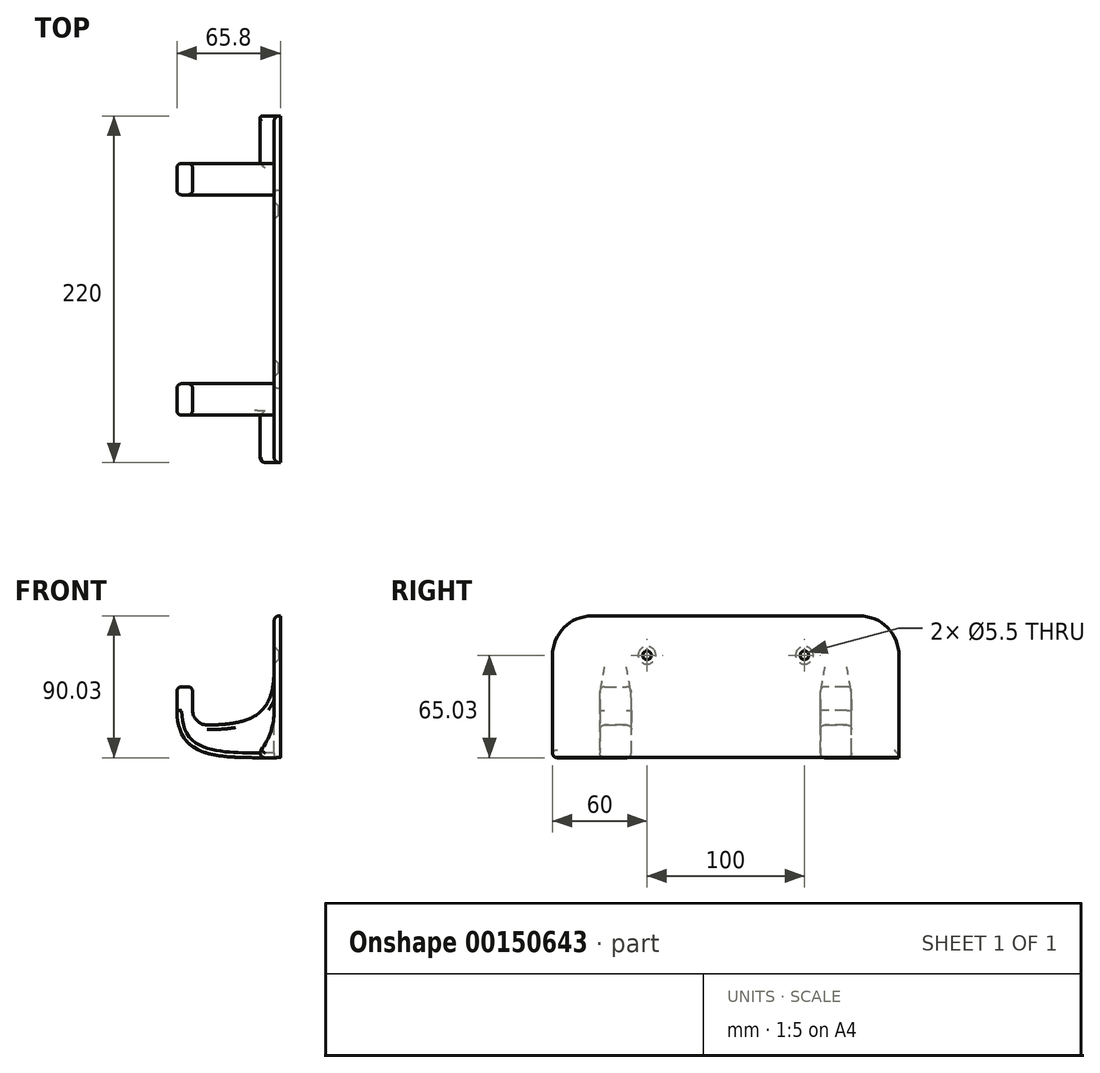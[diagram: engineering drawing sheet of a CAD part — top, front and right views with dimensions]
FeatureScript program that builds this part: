
annotation { "Feature Type Name" : "Feature", "Feature Type Description" : "" }
export const myFeature = defineFeature(function(context is Context, id is Id, definition is map)
    precondition{}
    {
        {
            var Q0;
            Q0=qCreatedBy(makeId("Front.planeOp"),FACE);
            var sketch = newSketch(context, id + "F0", { "sketchPlane" : qUnion([Q0])});
            skCircle(sketch, "E0", {"center": v(0, 0) * mm, "radius": 42.6 * mm});
            skLineSegment(sketch, "E1.bottom", {"start": v(36.6, 60) * mm, "end": v(46.6, 60) * mm});
            skLineSegment(sketch, "E1.top", {"start": v(36.6, -30) * mm, "end": v(46.6, -30) * mm});
            skLineSegment(sketch, "E1.left", {"start": v(36.6, 60) * mm, "end": v(36.6, -30) * mm});
            skLineSegment(sketch, "E1.right", {"start": v(46.6, 60) * mm, "end": v(46.6, -30) * mm});
            skCircle(sketch, "E2", {"center": v(0, 0) * mm, "radius": 9.2 * mm});
            skCircle(sketch, "E3", {"center": v(0, 0) * mm, "radius": 19.2 * mm});
            skLineSegment(sketch, "E4.bottom", {"start": v(-9.2, 0) * mm, "end": v(-19.2, 0) * mm});
            skLineSegment(sketch, "E4.top", {"start": v(-9.2, 15) * mm, "end": v(-19.2, 15) * mm});
            skLineSegment(sketch, "E4.left", {"start": v(-9.2, 0) * mm, "end": v(-9.2, 15) * mm});
            skLineSegment(sketch, "E4.right", {"start": v(-19.2, 0) * mm, "end": v(-19.2, 15) * mm});
            skFitSpline(sketch, "E5", {"points": [v(-19.2, 0) * mm, v(46.6, -30) * mm], "startDerivative": vector(1.42, -96.29) * mm, "endDerivative": vector(113.93, 0.01) * mm});
            skFitSpline(sketch, "E6", {"points": [v(0, -9.2) * mm, v(42.6, 27.48) * mm], "startDerivative": vector(97.7, -0.06) * mm, "endDerivative": vector(0, 82.45) * mm});
            skLineSegment(sketch, "E7", {"start": v(42.6, -30) * mm, "end": v(42.6, 60) * mm});
            skLineSegment(sketch, "E8", {"start": v(42.6, 27.48) * mm, "end": v(46.6, 27.48) * mm});
            skSolve(sketch);
        }
        {
            var Q0;
            {var subQ5=sQuery(id+"F0.wireOp",EDGE,"E1.top");Q0=makeQuery(id+"F0.imprint","IMPRINT",FACE,{"disambiguationData":[TD([[makeQuery(id+"F0.imprint","IMPRINT",EDGE,{"derivedFrom":subQ5}),-1.0]])]});}
            var Q1;
            {var subQ0=sQuery(id+"F0.wireOp",EDGE,"E4.bottom");Q1=makeQuery(id+"F0.imprint","IMPRINT",FACE,{"disambiguationData":[TD([[makeQuery(id+"F0.imprint","IMPRINT",EDGE,{"derivedFrom":subQ0}),-1.0]])]});}
            var Q2;
            {var subQ0=sQuery(id+"F0.wireOp",EDGE,"E4.bottom");Q2=makeQuery(id+"F0.imprint","IMPRINT",FACE,{"disambiguationData":[TD([[makeQuery(id+"F0.imprint","IMPRINT",EDGE,{"derivedFrom":subQ0}),1.0]])]});}
            var Q3;
            {var subQ0=sQuery(id+"F0.wireOp",EDGE,"E4.right");Q3=makeQuery(id+"F0.imprint","IMPRINT",FACE,{"disambiguationData":[TD([[makeQuery(id+"F0.imprint","IMPRINT",EDGE,{"derivedFrom":subQ0}),-1.0]])]});}
            var Q4;
            {var subQ0=sQuery(id+"F0.wireOp",EDGE,"E5");var subQ1=sQuery(id+"F0.wireOp",EDGE,"E0");var subQ2=makeQuery(id+"F0.imprint","INTERSECT",VERTEX,{"derivedFrom":[subQ1,subQ0]});Q4=makeQuery(id+"F0.imprint","IMPRINT",FACE,{"disambiguationData":[TD([[makeQuery(id+"F0.imprint","IMPRINT",EDGE,{"disambiguationData":[TD([[subQ2,-1.0]])],"derivedFrom":subQ1}),1.0]])]});}
            var Q5;
            {var subQ0=sQuery(id+"F0.wireOp",EDGE,"E1.left");var subQ1=sQuery(id+"F0.wireOp",EDGE,"E0");var subQ2=makeQuery(id+"F0.imprint","INTERSECT",VERTEX,{"disambiguationData":[OD(1.0)],"derivedFrom":[subQ1,subQ0]});Q5=makeQuery(id+"F0.imprint","IMPRINT",FACE,{"disambiguationData":[TD([[makeQuery(id+"F0.imprint","IMPRINT",EDGE,{"disambiguationData":[TD([[subQ2,-1.0]])],"derivedFrom":subQ1}),1.0]])]});}
            var Q6;
            {var subQ1=sQuery(id+"F0.wireOp",EDGE,"E1.top");Q6=makeQuery(id+"F0.imprint","IMPRINT",FACE,{"disambiguationData":[TD([[makeQuery(id+"F0.imprint","IMPRINT",EDGE,{"derivedFrom":subQ1}),1.0]])]});}
            var Q7;
            {var subQ0=sQuery(id+"F0.wireOp",EDGE,"PEo4gAHr-p0HZ-2GxJ-d3O3-oEwRO6jKPe9i");Q7=makeQuery(id+"F0.imprint","IMPRINT",FACE,{"disambiguationData":[TD([[makeQuery(id+"F0.imprint","IMPRINT",EDGE,{"derivedFrom":subQ0}),-1.0]])]});}
            var Q8;
            {var subQ0=sQuery(id+"F0.wireOp",EDGE,"PEo4gAHr-p0HZ-2GxJ-d3O3-oEwRO6jKPe9i");var subQ1=sQuery(id+"F0.wireOp",EDGE,"E0");var subQ2=makeQuery(id+"F0.imprint","INTERSECT",VERTEX,{"derivedFrom":[subQ1,subQ0]});Q8=makeQuery(id+"F0.imprint","IMPRINT",FACE,{"disambiguationData":[TD([[makeQuery(id+"F0.imprint","IMPRINT",EDGE,{"disambiguationData":[TD([[subQ2,-1.0]])],"derivedFrom":subQ1}),-1.0]])]});}
            var Q9;
            {var subQ0=sQuery(id+"F0.wireOp",EDGE,"E8");Q9=makeQuery(id+"F0.imprint","IMPRINT",FACE,{"disambiguationData":[TD([[makeQuery(id+"F0.imprint","IMPRINT",EDGE,{"derivedFrom":subQ0}),-1.0]])]});}
            var Q10;
            {var subQ5=sQuery(id+"F0.wireOp",EDGE,"E8");Q10=makeQuery(id+"F0.imprint","IMPRINT",FACE,{"disambiguationData":[TD([[makeQuery(id+"F0.imprint","IMPRINT",EDGE,{"derivedFrom":subQ5}),1.0]])]});}
            extrude(context, id + "F1", {"entities" : qUnion([Q0, Q1, Q2, Q3, Q4, Q5, Q6, Q7, Q8, Q9, Q10]), "depth" : 20 * mm});
        }
        {
            var Q0;
            {var subQ0=sQuery(id+"F0.wireOp",EDGE,"PEo4gAHr-p0HZ-2GxJ-d3O3-oEwRO6jKPe9i");Q0=makeQuery(id+"F0.imprint","IMPRINT",FACE,{"disambiguationData":[TD([[makeQuery(id+"F0.imprint","IMPRINT",EDGE,{"derivedFrom":subQ0}),-1.0]])]});}
            var Q1;
            {var subQ1=sQuery(id+"F0.wireOp",EDGE,"E1.top");Q1=makeQuery(id+"F0.imprint","IMPRINT",FACE,{"disambiguationData":[TD([[makeQuery(id+"F0.imprint","IMPRINT",EDGE,{"derivedFrom":subQ1}),1.0]])]});}
            var Q2;
            {var subQ5=sQuery(id+"F0.wireOp",EDGE,"E1.top");Q2=makeQuery(id+"F0.imprint","IMPRINT",FACE,{"disambiguationData":[TD([[makeQuery(id+"F0.imprint","IMPRINT",EDGE,{"derivedFrom":subQ5}),-1.0]])]});}
            var Q3;
            {var subQ4=sQuery(id+"F0.wireOp",EDGE,"E1.right");Q3=makeQuery(id+"F0.imprint","IMPRINT",FACE,{"disambiguationData":[TD([[makeQuery(id+"F0.imprint","IMPRINT",EDGE,{"derivedFrom":subQ4}),-1.0]])]});}
            var Q4;
            {var subQ0=sQuery(id+"F0.wireOp",EDGE,"E8");Q4=makeQuery(id+"F0.imprint","IMPRINT",FACE,{"disambiguationData":[TD([[makeQuery(id+"F0.imprint","IMPRINT",EDGE,{"derivedFrom":subQ0}),-1.0]])]});}
            extrude(context, id + "F2", {"entities" : qUnion([Q0, Q1, Q2, Q3, Q4]), "operationType" : NewBodyOperationType.ADD, "depth" : 50 * mm});
        }
        {
            var Q0;
            {var subQ0=sQuery(id+"F0.wireOp",EDGE,"E8");Q0=makeQuery(id+"F0.imprint","IMPRINT",FACE,{"disambiguationData":[TD([[makeQuery(id+"F0.imprint","IMPRINT",EDGE,{"derivedFrom":subQ0}),-1.0]])]});}
            var Q1;
            {var subQ5=sQuery(id+"F0.wireOp",EDGE,"E8");Q1=makeQuery(id+"F0.imprint","IMPRINT",FACE,{"disambiguationData":[TD([[makeQuery(id+"F0.imprint","IMPRINT",EDGE,{"derivedFrom":subQ5}),1.0]])]});}
            extrude(context, id + "F3", {"entities" : qUnion([Q0, Q1]), "operationType" : NewBodyOperationType.ADD, "oppositeDirection" : true, "depth" : 60 * mm});
        }
        {
            var Q0;
            Q0=makeQuery(id+"F1.opExtrude","SWEPT_BODY",BODY,{"disambiguationData":[OSD([sQuery(id+"F0.wireOp",EDGE,"E1.top"),sQuery(id+"F0.wireOp",EDGE,"E2"),sQuery(id+"F0.wireOp",EDGE,"E4.top"),sQuery(id+"F0.wireOp",EDGE,"E4.left"),sQuery(id+"F0.wireOp",EDGE,"E4.right"),sQuery(id+"F0.wireOp",EDGE,"E5"),sQuery(id+"F0.wireOp",EDGE,"E6"),sQuery(id+"F0.wireOp",EDGE,"E7")])]});
            var Q1;
            Q1=makeQuery(id+"F3.opExtrude","CAP_FACE",FACE,{"disambiguationData":[OSD([sQuery(id+"F0.wireOp",EDGE,"E1.bottom"),sQuery(id+"F0.wireOp",EDGE,"E1.top"),sQuery(id+"F0.wireOp",EDGE,"E1.right"),sQuery(id+"F0.wireOp",EDGE,"E7")])],"isStart":false});
            mirror(context, id + "F4", {"operationType" : NewBodyOperationType.ADD, "entities" : qUnion([Q0]), "mirrorPlane" : qUnion([Q1])});
        }
        {
            var Q0;
            {var subQ0=sQuery(id+"F0.wireOp",EDGE,"E7");var subQ1=sQuery(id+"F0.wireOp",EDGE,"E1.bottom");var subQ2=makeQuery(id+"F3.boolean.opBoolean","MERGE",EDGE,{"derivedFrom":[makeQuery(id+"F2.opExtrude","SWEPT_EDGE",EDGE,{"disambiguationData":[OSD([subQ1,subQ0])]}),makeQuery(id+"F3.opExtrude","SWEPT_EDGE",EDGE,{"disambiguationData":[OSD([subQ1,subQ0])]})]});Q0=makeQuery(id+"F4.boolean.opBoolean","MERGE",EDGE,{"derivedFrom":[subQ2,makeQuery(id+"F4.opPattern","COPY",EDGE,{"derivedFrom":subQ2,"instanceName":"1"})]});}
            var Q1;
            Q1=makeQuery(id+"F4.opPattern","COPY",EDGE,{"derivedFrom":makeQuery(id+"F2.opExtrude","CAP_EDGE",EDGE,{"disambiguationData":[OSD([sQuery(id+"F0.wireOp",EDGE,"E0")])],"isStart":false}),"instanceName":"1"});
            var Q2;
            Q2=makeQuery(id+"F4.opPattern","COPY",EDGE,{"derivedFrom":makeQuery(id+"F2.opExtrude","CAP_EDGE",EDGE,{"disambiguationData":[OSD([sQuery(id+"F0.wireOp",EDGE,"E7")])],"isStart":false}),"instanceName":"1"});
            var Q3;
            Q3=makeQuery(id+"F2.opExtrude","CAP_EDGE",EDGE,{"disambiguationData":[OSD([sQuery(id+"F0.wireOp",EDGE,"E7")])],"isStart":false});
            var Q4;
            Q4=makeQuery(id+"F2.opExtrude","CAP_EDGE",EDGE,{"disambiguationData":[OSD([sQuery(id+"F0.wireOp",EDGE,"E0")])],"isStart":false});
            var Q5;
            Q5=makeQuery(id+"F1.opExtrude","CAP_EDGE",EDGE,{"disambiguationData":[OSD([sQuery(id+"F0.wireOp",EDGE,"E6")])],"isStart":false});
            var Q6;
            Q6=makeQuery(id+"F1.opExtrude","CAP_EDGE",EDGE,{"disambiguationData":[OSD([sQuery(id+"F0.wireOp",EDGE,"E5")])],"isStart":false});
            var Q7;
            Q7=makeQuery(id+"F4.opPattern","COPY",EDGE,{"derivedFrom":makeQuery(id+"F2.opExtrude","SWEPT_EDGE",EDGE,{"disambiguationData":[OSD([sQuery(id+"F0.wireOp",EDGE,"E0"),sQuery(id+"F0.wireOp",EDGE,"E5")])]}),"instanceName":"1"});
            var Q8;
            Q8=makeQuery(id+"F4.opPattern","COPY",EDGE,{"derivedFrom":makeQuery(id+"F1.opExtrude","CAP_EDGE",EDGE,{"disambiguationData":[OSD([sQuery(id+"F0.wireOp",EDGE,"E5")])],"isStart":false}),"instanceName":"1"});
            var Q9;
            Q9=makeQuery(id+"F4.opPattern","COPY",EDGE,{"derivedFrom":makeQuery(id+"F1.opExtrude","CAP_EDGE",EDGE,{"disambiguationData":[OSD([sQuery(id+"F0.wireOp",EDGE,"E6")])],"isStart":true}),"instanceName":"1"});
            var Q10;
            Q10=makeQuery(id+"F4.opPattern","COPY",EDGE,{"derivedFrom":makeQuery(id+"F1.opExtrude","SWEPT_EDGE",EDGE,{"disambiguationData":[OSD([sQuery(id+"F0.wireOp",EDGE,"E4.top"),sQuery(id+"F0.wireOp",EDGE,"E4.right")])]}),"instanceName":"1"});
            var Q11;
            Q11=makeQuery(id+"F4.opPattern","COPY",EDGE,{"derivedFrom":makeQuery(id+"F1.opExtrude","CAP_EDGE",EDGE,{"disambiguationData":[OSD([sQuery(id+"F0.wireOp",EDGE,"E6")])],"isStart":false}),"instanceName":"1"});
            var Q12;
            Q12=makeQuery(id+"F4.opPattern","COPY",EDGE,{"derivedFrom":makeQuery(id+"F1.opExtrude","SWEPT_EDGE",EDGE,{"disambiguationData":[OSD([sQuery(id+"F0.wireOp",EDGE,"E4.top"),sQuery(id+"F0.wireOp",EDGE,"E4.left")])]}),"instanceName":"1"});
            var Q13;
            Q13=makeQuery(id+"F1.opExtrude","SWEPT_EDGE",EDGE,{"disambiguationData":[OSD([sQuery(id+"F0.wireOp",EDGE,"E4.top"),sQuery(id+"F0.wireOp",EDGE,"E4.right")])]});
            fillet(context, id + "F5", {"entities" : qUnion([Q0, Q1, Q2, Q3, Q4, Q5, Q6, Q7, Q8, Q9, Q10, Q11, Q12, Q13]), "radius" : 3 * mm, "tangentPropagation" : true, "allowEdgeOverflow" : false});
        }
        {
            var Q0;
            {var subQ0=sQuery(id+"F0.wireOp",EDGE,"E7");var subQ1=sQuery(id+"F0.wireOp",EDGE,"E5");var subQ2=sQuery(id+"F0.wireOp",EDGE,"E4.right");Q0=makeQuery(id+"F4.opPattern","COPY",EDGE,{"derivedFrom":makeQuery(id+"F2.boolean.opBoolean","SPLIT",EDGE,{"disambiguationData":[TD([makeQuery(id+"F1.opExtrude","CAP_FACE",FACE,{"disambiguationData":[OSD([sQuery(id+"F0.wireOp",EDGE,"E1.top"),sQuery(id+"F0.wireOp",EDGE,"E2"),sQuery(id+"F0.wireOp",EDGE,"E4.top"),sQuery(id+"F0.wireOp",EDGE,"E4.left"),subQ2,subQ1,sQuery(id+"F0.wireOp",EDGE,"E6"),subQ0])],"isStart":true}),makeQuery(id+"F1.opExtrude","SWEPT_FACE",FACE,{"disambiguationData":[OSD([subQ2])]}),makeQuery(id+"F1.opExtrude","SWEPT_FACE",FACE,{"disambiguationData":[OSD([subQ1])]}),makeQuery(id+"F2.opExtrude","CAP_FACE",FACE,{"disambiguationData":[OSD([sQuery(id+"F0.wireOp",EDGE,"E0"),sQuery(id+"F0.wireOp",EDGE,"E1.bottom"),sQuery(id+"F0.wireOp",EDGE,"E1.right"),subQ1,subQ0])],"isStart":true}),makeQuery(id+"F2.opExtrude","SWEPT_FACE",FACE,{"disambiguationData":[OSD([subQ1])]})])],"derivedFrom":makeQuery(id+"F1.opExtrude","CAP_EDGE",EDGE,{"disambiguationData":[OSD([subQ1])],"isStart":true})}),"instanceName":"1"});}
            var Q1;
            Q1=makeQuery(id+"F4.opPattern","COPY",EDGE,{"derivedFrom":makeQuery(id+"F1.opExtrude","CAP_EDGE",EDGE,{"disambiguationData":[OSD([sQuery(id+"F0.wireOp",EDGE,"E4.top")])],"isStart":true}),"instanceName":"1"});
            var Q2;
            Q2=makeQuery(id+"F4.opPattern","COPY",EDGE,{"derivedFrom":makeQuery(id+"F1.opExtrude","CAP_EDGE",EDGE,{"disambiguationData":[OSD([sQuery(id+"F0.wireOp",EDGE,"E4.top")])],"isStart":false}),"instanceName":"1"});
            var Q3;
            Q3=makeQuery(id+"F1.opExtrude","CAP_EDGE",EDGE,{"disambiguationData":[OSD([sQuery(id+"F0.wireOp",EDGE,"E4.top")])],"isStart":false});
            var Q4;
            Q4=makeQuery(id+"F1.opExtrude","CAP_EDGE",EDGE,{"disambiguationData":[OSD([sQuery(id+"F0.wireOp",EDGE,"E6")])],"isStart":true});
            var Q5;
            {var subQ0=sQuery(id+"F0.wireOp",EDGE,"E7");var subQ1=sQuery(id+"F0.wireOp",EDGE,"E5");var subQ2=sQuery(id+"F0.wireOp",EDGE,"E4.right");Q5=makeQuery(id+"F2.boolean.opBoolean","SPLIT",EDGE,{"disambiguationData":[TD([makeQuery(id+"F1.opExtrude","CAP_FACE",FACE,{"disambiguationData":[OSD([sQuery(id+"F0.wireOp",EDGE,"E1.top"),sQuery(id+"F0.wireOp",EDGE,"E2"),sQuery(id+"F0.wireOp",EDGE,"E4.top"),sQuery(id+"F0.wireOp",EDGE,"E4.left"),subQ2,subQ1,sQuery(id+"F0.wireOp",EDGE,"E6"),subQ0])],"isStart":true}),makeQuery(id+"F1.opExtrude","SWEPT_FACE",FACE,{"disambiguationData":[OSD([subQ2])]}),makeQuery(id+"F1.opExtrude","SWEPT_FACE",FACE,{"disambiguationData":[OSD([subQ1])]}),makeQuery(id+"F2.opExtrude","CAP_FACE",FACE,{"disambiguationData":[OSD([sQuery(id+"F0.wireOp",EDGE,"E0"),sQuery(id+"F0.wireOp",EDGE,"E1.bottom"),sQuery(id+"F0.wireOp",EDGE,"E1.right"),subQ1,subQ0])],"isStart":true}),makeQuery(id+"F2.opExtrude","SWEPT_FACE",FACE,{"disambiguationData":[OSD([subQ1])]})])],"derivedFrom":makeQuery(id+"F1.opExtrude","CAP_EDGE",EDGE,{"disambiguationData":[OSD([subQ1])],"isStart":true})});}
            var Q6;
            Q6=makeQuery(id+"F1.opExtrude","CAP_EDGE",EDGE,{"disambiguationData":[OSD([sQuery(id+"F0.wireOp",EDGE,"E4.top")])],"isStart":true});
            var Q7;
            Q7=makeQuery(id+"F2.opExtrude","SWEPT_EDGE",EDGE,{"disambiguationData":[OSD([sQuery(id+"F0.wireOp",EDGE,"E0"),sQuery(id+"F0.wireOp",EDGE,"E5")])]});
            fillet(context, id + "F6", {"entities" : qUnion([Q0, Q1, Q2, Q3, Q4, Q5, Q6, Q7]), "radius" : 3 * mm, "tangentPropagation" : true, "allowEdgeOverflow" : false});
        }
        {
            var Q0;
            Q0=makeQuery(id+"F4.opPattern","COPY",EDGE,{"derivedFrom":makeQuery(id+"F2.opExtrude","CAP_EDGE",EDGE,{"disambiguationData":[OSD([sQuery(id+"F0.wireOp",EDGE,"E1.bottom")])],"isStart":false}),"instanceName":"1"});
            var Q1;
            Q1=makeQuery(id+"F2.opExtrude","CAP_EDGE",EDGE,{"disambiguationData":[OSD([sQuery(id+"F0.wireOp",EDGE,"E1.bottom")])],"isStart":false});
            fillet(context, id + "F7", {"entities" : qUnion([Q0, Q1]), "radius" : 25 * mm, "tangentPropagation" : true, "allowEdgeOverflow" : false});
        }
        {
            var Q0;
            {var subQ0=sQuery(id+"F0.wireOp",EDGE,"E7");var subQ1=makeQuery(id+"F3.boolean.opBoolean","MERGE",FACE,{"derivedFrom":[makeQuery(id+"F2.boolean.opBoolean","MERGE",FACE,{"derivedFrom":[makeQuery(id+"F1.opExtrude","SWEPT_FACE",FACE,{"disambiguationData":[OSD([subQ0])]}),makeQuery(id+"F2.opExtrude","SWEPT_FACE",FACE,{"disambiguationData":[OSD([subQ0])]})]}),makeQuery(id+"F3.opExtrude","SWEPT_FACE",FACE,{"disambiguationData":[OSD([subQ0])]})]});Q0=makeQuery(id+"F4.boolean.opBoolean","MERGE",FACE,{"derivedFrom":[subQ1,makeQuery(id+"F4.opPattern","COPY",FACE,{"derivedFrom":subQ1,"instanceName":"1"})]});}
            var sketch = newSketch(context, id + "F8", { "sketchPlane" : qUnion([Q0])});
            skLineSegment(sketch, "E9", {"start": v(-167, 35) * mm, "end": v(47, 35) * mm});
            skPoint(sketch, "E10", {"position": v(-110, 35) * mm});
            skPoint(sketch, "E11", {"position": v(-10, 35) * mm});
            skSolve(sketch);
        }
        {
            var Q0;
            Q0=sQuery(id+"F8.wireOp",VERTEX,"E10");
            var Q1;
            Q1=sQuery(id+"F8.wireOp",VERTEX,"E11");
            var Q2;
            Q2=makeQuery(id+"F1.opExtrude","SWEPT_BODY",BODY,{"disambiguationData":[OSD([sQuery(id+"F0.wireOp",EDGE,"E1.bottom"),sQuery(id+"F0.wireOp",EDGE,"E1.right"),sQuery(id+"F0.wireOp",EDGE,"E2"),sQuery(id+"F0.wireOp",EDGE,"E4.top"),sQuery(id+"F0.wireOp",EDGE,"E4.left"),sQuery(id+"F0.wireOp",EDGE,"E4.right"),sQuery(id+"F0.wireOp",EDGE,"E5"),sQuery(id+"F0.wireOp",EDGE,"E6"),sQuery(id+"F0.wireOp",EDGE,"E7")])]});
            hole(context, id + "F9", {"style" : HoleStyle.C_SINK, "endStyle" : HoleEndStyle.THROUGH, "standardTappedOrClearance" : lookupTablePath({ "standard" : "ISO", "fit" : "Normal", "size" : "M5", "type" : "Clearance" }), "standardBlindInLast" : lookupTablePath({ "fit" : "Standard", "standard" : "ISO", "size" : "M5", "type" : "Clearance" }), "holeDiameter" : 5.5 * mm, "cSinkDiameter" : 11.2 * mm, "cSinkAngle" : 90 * degree, "locations" : qUnion([Q0, Q1]), "scope" : qUnion([Q2]), "isTappedThrough" : true});
        }
        {
            var Q0;
            {var subQ0=makeQuery(id+"F3.opExtrude","SWEPT_EDGE",EDGE,{"disambiguationData":[OSD([sQuery(id+"F0.wireOp",EDGE,"E1.top"),sQuery(id+"F0.wireOp",EDGE,"E7")])]});Q0=makeQuery(id+"F4.boolean.opBoolean","MERGE",EDGE,{"derivedFrom":[subQ0,makeQuery(id+"F4.opPattern","COPY",EDGE,{"derivedFrom":subQ0,"instanceName":"1"})]});}
            fillet(context, id + "F10", {"entities" : qUnion([Q0]), "radius" : 1 * mm, "tangentPropagation" : true, "allowEdgeOverflow" : false});
        }
    });
